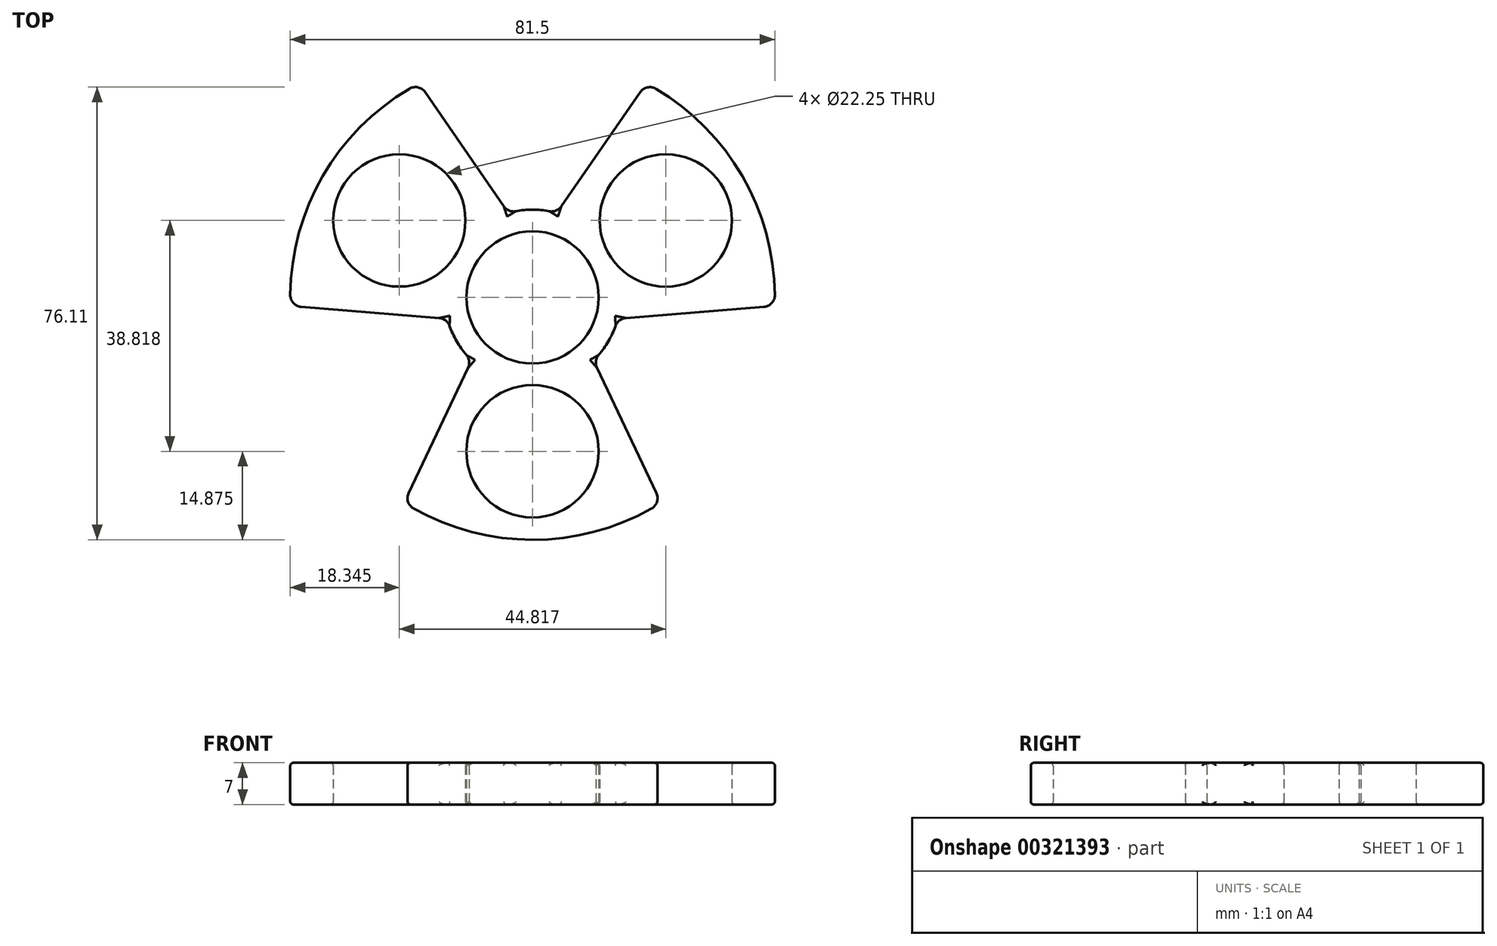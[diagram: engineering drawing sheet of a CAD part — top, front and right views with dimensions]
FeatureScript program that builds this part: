
annotation { "Feature Type Name" : "Feature", "Feature Type Description" : "" }
export const myFeature = defineFeature(function(context is Context, id is Id, definition is map)
    precondition{}
    {
        {
            var Q0;
            Q0=qCreatedBy(makeId("Top.planeOp"),FACE);
            var sketch = newSketch(context, id + "F0", { "sketchPlane" : qUnion([Q0])});
            skCircle(sketch, "E0", {"center": v(0, 0) * mm, "radius": 11.12 * mm});
            skCircle(sketch, "E1", {"center": v(0, 0) * mm, "radius": 14.75 * mm});
            skPoint(sketch, "E2", {"position": v(10.25, -10.6) * mm});
            skPoint(sketch, "E3", {"position": v(-10.25, -10.6) * mm});
            skPoint(sketch, "E4", {"position": v(-21.63, -34.54) * mm});
            skPoint(sketch, "E5", {"position": v(21.6, -34.55) * mm});
            skLineSegment(sketch, "E6", {"start": v(-10.25, -10.6) * mm, "end": v(-21.63, -34.54) * mm});
            skLineSegment(sketch, "E7", {"start": v(10.25, -10.6) * mm, "end": v(21.6, -34.55) * mm});
            skArc(sketch, "E8", {"start": v(21.6, -34.55) * mm, "mid": v(-0.01, -40.75) * mm, "end": v(-21.63, -34.54) * mm});
            skPoint(sketch, "E9", {"position": v(0, -10.6) * mm});
            skPoint(sketch, "E10", {"position": v(0, -11.12) * mm});
            skPoint(sketch, "E11", {"position": v(0, -14.75) * mm});
            skPoint(sketch, "E12.endSnap0", {"position": v(-0.01, -40.75) * mm});
            skPoint(sketch, "E13", {"position": v(0, -37) * mm});
            skPoint(sketch, "E14", {"position": v(0, -25.87) * mm});
            skCircle(sketch, "E15", {"center": v(0, -25.87) * mm, "radius": 11.13 * mm});
            skArc(sketch, "E16.1.0", {"start": v(19.12, 35.99) * mm, "mid": v(35.3, 20.37) * mm, "end": v(40.72, -1.46) * mm});
            skLineSegment(sketch, "E16.1.1", {"start": v(4.06, 14.18) * mm, "end": v(19.12, 35.99) * mm});
            skLineSegment(sketch, "E16.1.2", {"start": v(14.31, -3.57) * mm, "end": v(40.72, -1.46) * mm});
            skCircle(sketch, "E16.1.3", {"center": v(22.41, 12.93) * mm, "radius": 11.13 * mm});
            skArc(sketch, "E16.2.0", {"start": v(-40.72, -1.44) * mm, "mid": v(-35.29, 20.38) * mm, "end": v(-19.1, 36) * mm});
            skLineSegment(sketch, "E16.2.1", {"start": v(-14.31, -3.57) * mm, "end": v(-40.72, -1.44) * mm});
            skLineSegment(sketch, "E16.2.2", {"start": v(-4.06, 14.18) * mm, "end": v(-19.1, 36) * mm});
            skCircle(sketch, "E16.2.3", {"center": v(-22.4, 12.94) * mm, "radius": 11.13 * mm});
            skSolve(sketch);
        }
        {
            var Q0;
            Q0=qSketchRegion(id+"F0",true);
            extrude(context, id + "F1", {"entities" : qUnion([Q0]), "depth" : 7 * mm});
        }
        {
            var Q0;
            Q0=makeQuery(id+"F1.opExtrude","SWEPT_EDGE",EDGE,{"disambiguationData":[OSD([sQuery(id+"F0.wireOp",EDGE,"E7"),sQuery(id+"F0.wireOp",EDGE,"E8")])]});
            var Q1;
            Q1=makeQuery(id+"F1.opExtrude","SWEPT_EDGE",EDGE,{"disambiguationData":[OSD([sQuery(id+"F0.wireOp",EDGE,"E6"),sQuery(id+"F0.wireOp",EDGE,"E8")])]});
            var Q2;
            Q2=makeQuery(id+"F1.opExtrude","SWEPT_EDGE",EDGE,{"disambiguationData":[OSD([sQuery(id+"F0.wireOp",EDGE,"E16.2.0"),sQuery(id+"F0.wireOp",EDGE,"E16.2.1")])]});
            var Q3;
            Q3=makeQuery(id+"F1.opExtrude","SWEPT_EDGE",EDGE,{"disambiguationData":[OSD([sQuery(id+"F0.wireOp",EDGE,"E16.2.0"),sQuery(id+"F0.wireOp",EDGE,"E16.2.2")])]});
            var Q4;
            Q4=makeQuery(id+"F1.opExtrude","SWEPT_EDGE",EDGE,{"disambiguationData":[OSD([sQuery(id+"F0.wireOp",EDGE,"E16.1.0"),sQuery(id+"F0.wireOp",EDGE,"E16.1.1")])]});
            var Q5;
            Q5=makeQuery(id+"F1.opExtrude","SWEPT_EDGE",EDGE,{"disambiguationData":[OSD([sQuery(id+"F0.wireOp",EDGE,"E16.1.0"),sQuery(id+"F0.wireOp",EDGE,"E16.1.2")])]});
            fillet(context, id + "F2", {"entities" : qUnion([Q0, Q1, Q2, Q3, Q4, Q5]), "radius" : 2 * mm, "tangentPropagation" : true, "allowEdgeOverflow" : false});
        }
        {
            var Q0;
            Q0=makeQuery(id+"F1.opExtrude","CAP_FACE",FACE,{"disambiguationData":[OSD([sQuery(id+"F0.wireOp",EDGE,"E0"),sQuery(id+"F0.wireOp",EDGE,"E1"),sQuery(id+"F0.wireOp",EDGE,"E6"),sQuery(id+"F0.wireOp",EDGE,"E7"),sQuery(id+"F0.wireOp",EDGE,"E8"),sQuery(id+"F0.wireOp",EDGE,"E15"),sQuery(id+"F0.wireOp",EDGE,"E16.1.0"),sQuery(id+"F0.wireOp",EDGE,"E16.1.1"),sQuery(id+"F0.wireOp",EDGE,"E16.1.2"),sQuery(id+"F0.wireOp",EDGE,"E16.1.3"),sQuery(id+"F0.wireOp",EDGE,"E16.2.0"),sQuery(id+"F0.wireOp",EDGE,"E16.2.1"),sQuery(id+"F0.wireOp",EDGE,"E16.2.2"),sQuery(id+"F0.wireOp",EDGE,"E16.2.3")])],"isStart":true});
            var Q1;
            Q1=makeQuery(id+"F1.opExtrude","CAP_FACE",FACE,{"disambiguationData":[OSD([sQuery(id+"F0.wireOp",EDGE,"E0"),sQuery(id+"F0.wireOp",EDGE,"E1"),sQuery(id+"F0.wireOp",EDGE,"E6"),sQuery(id+"F0.wireOp",EDGE,"E7"),sQuery(id+"F0.wireOp",EDGE,"E8"),sQuery(id+"F0.wireOp",EDGE,"E15"),sQuery(id+"F0.wireOp",EDGE,"E16.1.0"),sQuery(id+"F0.wireOp",EDGE,"E16.1.1"),sQuery(id+"F0.wireOp",EDGE,"E16.1.2"),sQuery(id+"F0.wireOp",EDGE,"E16.1.3"),sQuery(id+"F0.wireOp",EDGE,"E16.2.0"),sQuery(id+"F0.wireOp",EDGE,"E16.2.1"),sQuery(id+"F0.wireOp",EDGE,"E16.2.2"),sQuery(id+"F0.wireOp",EDGE,"E16.2.3")])],"isStart":false});
            fillet(context, id + "F3", {"entities" : qUnion([Q0, Q1]), "radius" : .5 * mm, "tangentPropagation" : true, "allowEdgeOverflow" : false});
        }
        {
            var Q0;
            Q0=makeQuery(id+"F1.opExtrude","SWEPT_EDGE",EDGE,{"disambiguationData":[OSD([sQuery(id+"F0.wireOp",EDGE,"E1"),sQuery(id+"F0.wireOp",EDGE,"E16.2.2")])]});
            var Q1;
            Q1=makeQuery(id+"F1.opExtrude","SWEPT_EDGE",EDGE,{"disambiguationData":[OSD([sQuery(id+"F0.wireOp",EDGE,"E1"),sQuery(id+"F0.wireOp",EDGE,"E16.1.1")])]});
            var Q2;
            Q2=makeQuery(id+"F1.opExtrude","SWEPT_EDGE",EDGE,{"disambiguationData":[OSD([sQuery(id+"F0.wireOp",EDGE,"E1"),sQuery(id+"F0.wireOp",EDGE,"E16.1.2")])]});
            var Q3;
            Q3=makeQuery(id+"F1.opExtrude","SWEPT_EDGE",EDGE,{"disambiguationData":[OSD([sQuery(id+"F0.wireOp",EDGE,"E1"),sQuery(id+"F0.wireOp",EDGE,"E7")])]});
            var Q4;
            Q4=makeQuery(id+"F1.opExtrude","SWEPT_EDGE",EDGE,{"disambiguationData":[OSD([sQuery(id+"F0.wireOp",EDGE,"E1"),sQuery(id+"F0.wireOp",EDGE,"E6")])]});
            var Q5;
            Q5=makeQuery(id+"F1.opExtrude","SWEPT_EDGE",EDGE,{"disambiguationData":[OSD([sQuery(id+"F0.wireOp",EDGE,"E1"),sQuery(id+"F0.wireOp",EDGE,"E16.2.1")])]});
            fillet(context, id + "F4", {"entities" : qUnion([Q0, Q1, Q2, Q3, Q4, Q5]), "radius" : 2 * mm, "tangentPropagation" : true, "allowEdgeOverflow" : false});
        }
    });
